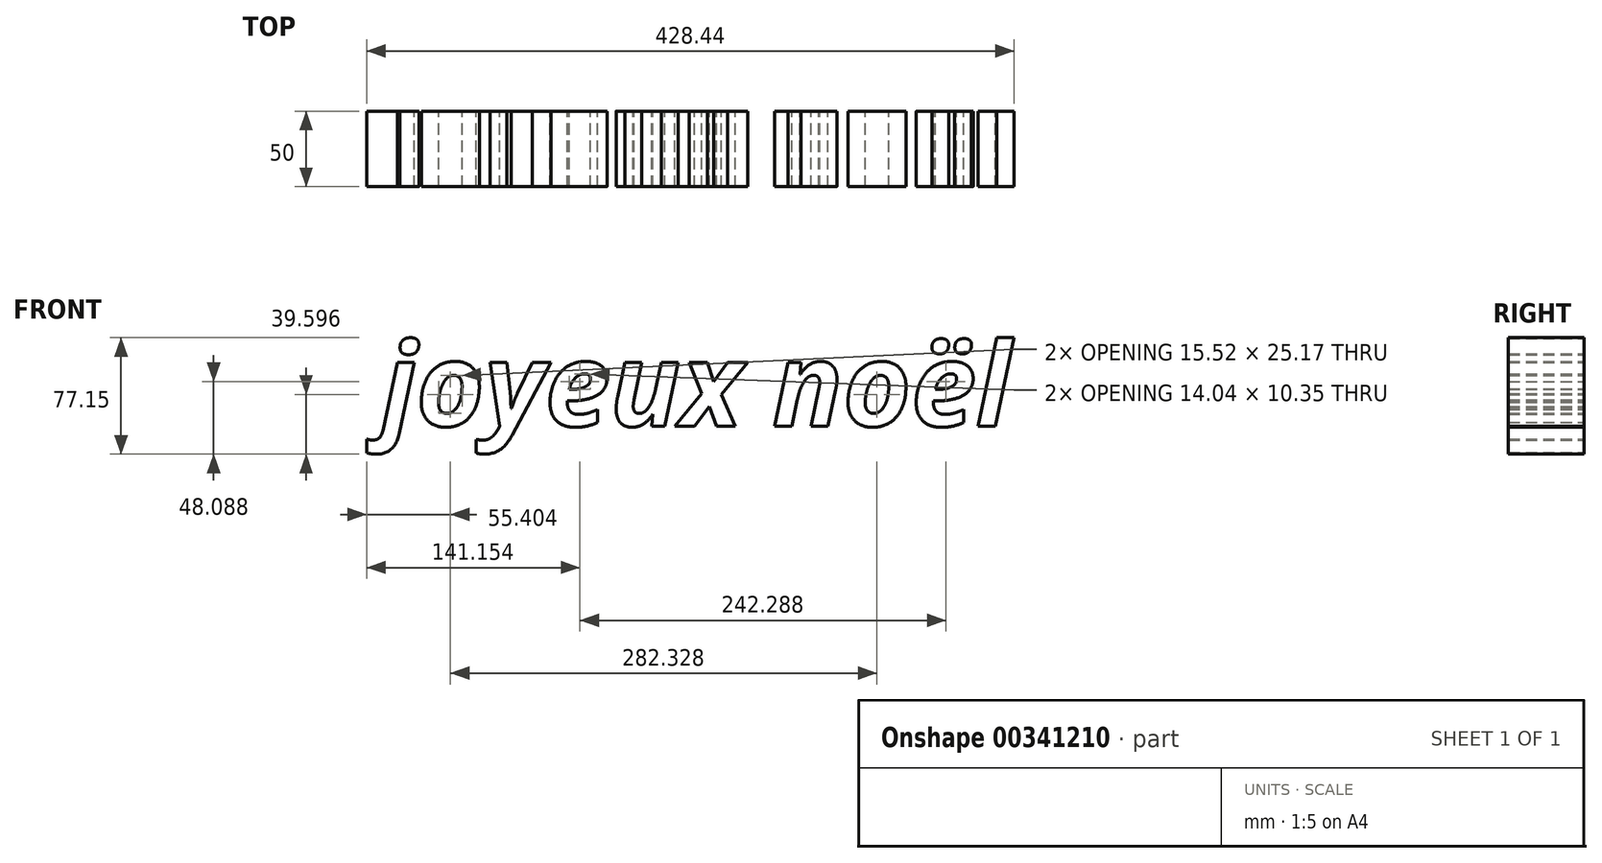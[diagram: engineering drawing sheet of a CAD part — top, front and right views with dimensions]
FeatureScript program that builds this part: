
annotation { "Feature Type Name" : "Feature", "Feature Type Description" : "" }
export const myFeature = defineFeature(function(context is Context, id is Id, definition is map)
    precondition{}
    {
        {
            var Q0;
            Q0=qCreatedBy(makeId("Front.planeOp"),FACE);
            var sketch = newSketch(context, id + "F0", { "sketchPlane" : qUnion([Q0])});
            skText(sketch, "E0", { "text": "joyeux noël", "fontName": "OpenSans-BoldItalic.ttf"});
            const initialGuessF0  = {"E0": [-0.43343, -0.05554, 1, 0, 0.05554]};
            skSetInitialGuess(sketch, initialGuessF0);
            skSolve(sketch);
        }
        {
            var Q0;
            Q0 = qSketchRegion(id + "F0", true);
            extrude(context, id + "F1", {"entities" : qUnion([Q0]), "depth" : 50 * mm});
        }
    });
